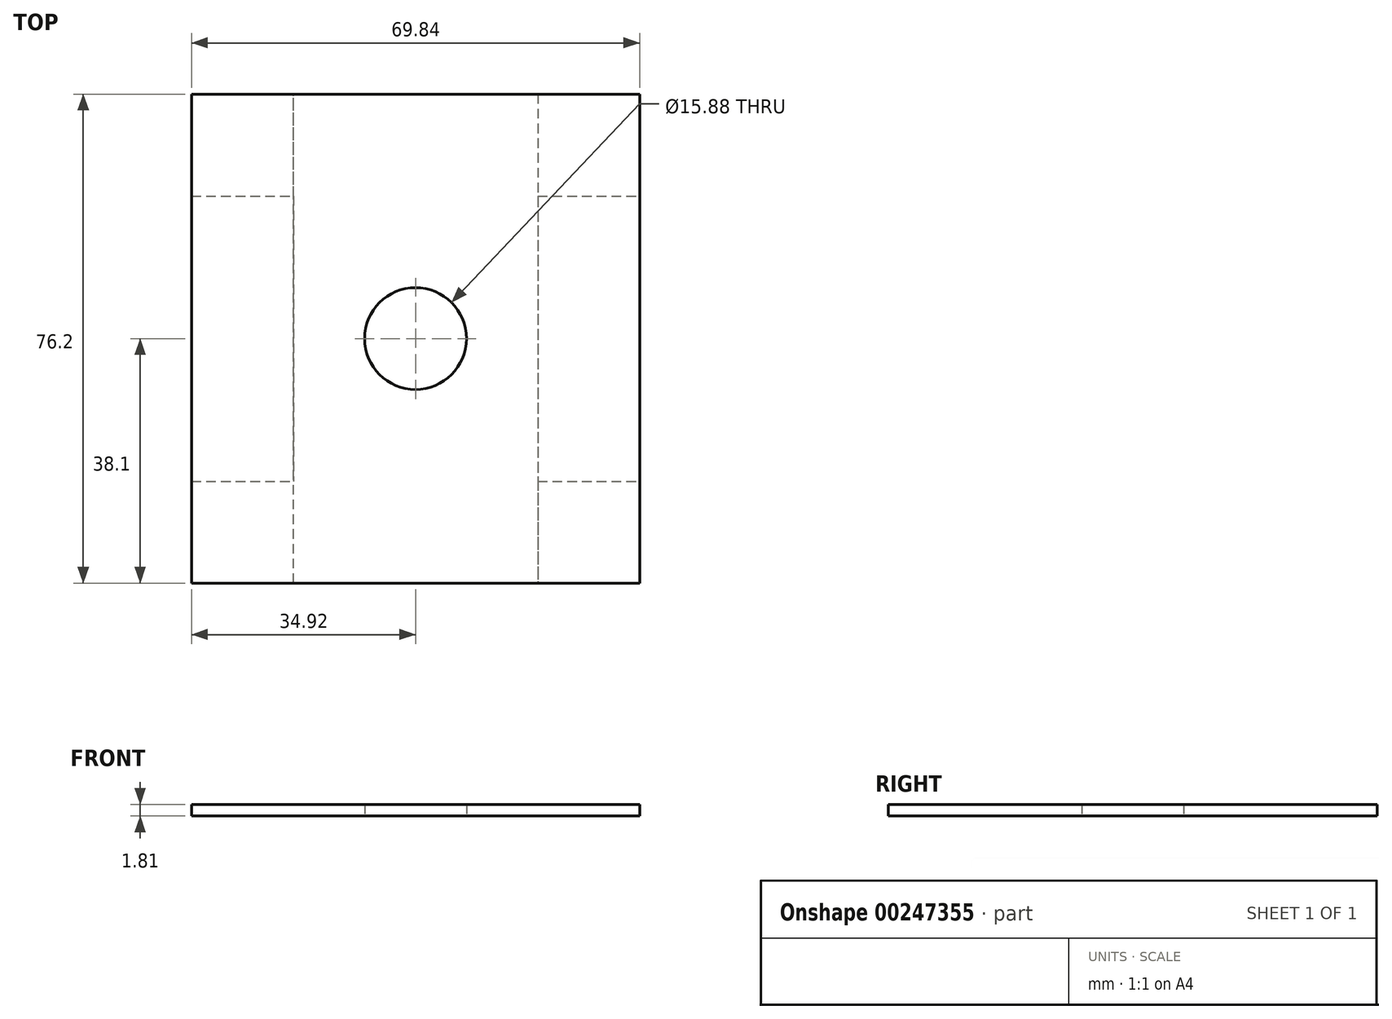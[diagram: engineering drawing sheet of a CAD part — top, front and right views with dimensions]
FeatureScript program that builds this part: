
annotation { "Feature Type Name" : "Feature", "Feature Type Description" : "" }
export const myFeature = defineFeature(function(context is Context, id is Id, definition is map)
    precondition{}
    {
        {
            var Q0;
            Q0=qCreatedBy(makeId("Top.planeOp"),FACE);
            var sketch = newSketch(context, id + "F0", { "sketchPlane" : qUnion([Q0])});
            skLineSegment(sketch, "E0.bottom", {"start": v(63.5, -38.1) * mm, "end": v(-63.5, -38.1) * mm});
            skLineSegment(sketch, "E0.top", {"start": v(34.93, 38.1) * mm, "end": v(19.05, 38.1) * mm});
            skLineSegment(sketch, "E0.left", {"start": v(63.5, -38.1) * mm, "end": v(63.5, -12.7) * mm});
            skLineSegment(sketch, "E0.right", {"start": v(-63.5, -38.1) * mm, "end": v(-63.5, -12.7) * mm});
            skPoint(sketch, "E0.middle", {"position": v(0, 0) * mm});
            skLineSegment(sketch, "E1", {"start": v(-63.5, 12.7) * mm, "end": v(-42.86, 12.7) * mm});
            skLineSegment(sketch, "E2", {"start": v(-42.86, 12.7) * mm, "end": v(-42.86, -12.7) * mm});
            skLineSegment(sketch, "E3", {"start": v(-42.86, -12.7) * mm, "end": v(-63.5, -12.7) * mm});
            skLineSegment(sketch, "E4", {"start": v(63.5, 12.7) * mm, "end": v(42.86, 12.7) * mm});
            skLineSegment(sketch, "E5", {"start": v(42.86, 12.7) * mm, "end": v(42.86, -12.7) * mm});
            skLineSegment(sketch, "E6", {"start": v(42.86, -12.7) * mm, "end": v(63.5, -12.7) * mm});
            skLineSegment(sketch, "E7.trimOffspring", {"start": v(-63.5, 12.7) * mm, "end": v(-63.5, 38.1) * mm});
            skLineSegment(sketch, "E8.trimOffspring", {"start": v(63.5, 12.7) * mm, "end": v(63.5, 38.1) * mm});
            skCircle(sketch, "E9", {"center": v(0, 0) * mm, "radius": 7.94 * mm});
            skLineSegment(sketch, "E10", {"start": v(-34.93, 38.1) * mm, "end": v(-34.93, 22.23) * mm});
            skLineSegment(sketch, "E11", {"start": v(-19.05, -38.1) * mm, "end": v(-19.05, -22.23) * mm});
            skLineSegment(sketch, "E12", {"start": v(19.05, 38.1) * mm, "end": v(19.05, 22.23) * mm});
            skLineSegment(sketch, "E13", {"start": v(34.92, 38.1) * mm, "end": v(34.92, 22.23) * mm});
            skLineSegment(sketch, "E14", {"start": v(-63.5, 38.1) * mm, "end": v(-34.93, 38.1) * mm});
            skLineSegment(sketch, "E15", {"start": v(34.93, 38.1) * mm, "end": v(63.5, 38.1) * mm});
            skLineSegment(sketch, "E16.trimOffspring", {"start": v(-19.05, 38.1) * mm, "end": v(-34.93, 38.1) * mm});
            skLineSegment(sketch, "E17", {"start": v(-19.05, 38.1) * mm, "end": v(19.05, 38.1) * mm});
            skLineSegment(sketch, "E18", {"start": v(-34.93, 22.22) * mm, "end": v(-19.05, 22.23) * mm});
            skLineSegment(sketch, "E19", {"start": v(-34.92, -22.23) * mm, "end": v(-19.05, -22.23) * mm});
            skLineSegment(sketch, "E20", {"start": v(19.05, -22.22) * mm, "end": v(34.92, -22.22) * mm});
            skLineSegment(sketch, "E21", {"start": v(19.05, 22.23) * mm, "end": v(34.92, 22.23) * mm});
            skLineSegment(sketch, "E22.trimOffspring", {"start": v(-34.92, -22.23) * mm, "end": v(-34.92, -38.1) * mm});
            skLineSegment(sketch, "E23.trimOffspring", {"start": v(-19.05, 22.23) * mm, "end": v(-19.05, 38.1) * mm});
            skLineSegment(sketch, "E24.trimOffspring", {"start": v(19.05, -22.22) * mm, "end": v(19.05, -38.1) * mm});
            skLineSegment(sketch, "E25.trimOffspring", {"start": v(34.92, -22.22) * mm, "end": v(34.92, -38.1) * mm});
            skLineSegment(sketch, "E26", {"start": v(-34.93, 22.22) * mm, "end": v(-34.92, -22.23) * mm});
            skLineSegment(sketch, "E27", {"start": v(-19.05, 22.23) * mm, "end": v(-19.05, -22.23) * mm});
            skLineSegment(sketch, "E28", {"start": v(19.05, 22.23) * mm, "end": v(19.05, -22.22) * mm});
            skLineSegment(sketch, "E29", {"start": v(34.92, 22.23) * mm, "end": v(34.92, -22.22) * mm});
            skSolve(sketch);
        }
        {
            var Q0;
            Q0=makeQuery(id+"F0.imprint","IMPRINT",FACE,{"disambiguationData":[TD([[makeQuery(id+"F0.imprint","IMPRINT",EDGE,{"derivedFrom":sQuery(id+"F0.wireOp",EDGE,"E20")}),-1.0]])]});
            var Q1;
            Q1=makeQuery(id+"F0.imprint","IMPRINT",FACE,{"disambiguationData":[TD([[makeQuery(id+"F0.imprint","IMPRINT",EDGE,{"derivedFrom":sQuery(id+"F0.wireOp",EDGE,"E20")}),1.0]])]});
            var Q2;
            {var subQ0=sQuery(id+"F0.wireOp",EDGE,"E0.left");Q2=makeQuery(id+"F0.imprint","IMPRINT",FACE,{"disambiguationData":[TD([[makeQuery(id+"F0.imprint","IMPRINT",EDGE,{"derivedFrom":subQ0}),1.0]])]});}
            var Q3;
            Q3=makeQuery(id+"F0.imprint","IMPRINT",FACE,{"disambiguationData":[TD([[makeQuery(id+"F0.imprint","IMPRINT",EDGE,{"derivedFrom":sQuery(id+"F0.wireOp",EDGE,"E9")}),-1.0]])]});
            var Q4;
            {var subQ0=sQuery(id+"F0.wireOp",EDGE,"E11");Q4=makeQuery(id+"F0.imprint","IMPRINT",FACE,{"disambiguationData":[TD([[makeQuery(id+"F0.imprint","IMPRINT",EDGE,{"derivedFrom":subQ0}),1.0]])]});}
            var Q5;
            Q5=makeQuery(id+"F0.imprint","IMPRINT",FACE,{"disambiguationData":[TD([[makeQuery(id+"F0.imprint","IMPRINT",EDGE,{"derivedFrom":sQuery(id+"F0.wireOp",EDGE,"E0.top")}),1.0]])]});
            var Q6;
            {var subQ1=sQuery(id+"F0.wireOp",EDGE,"E0.right");Q6=makeQuery(id+"F0.imprint","IMPRINT",FACE,{"disambiguationData":[TD([[makeQuery(id+"F0.imprint","IMPRINT",EDGE,{"derivedFrom":subQ1}),-1.0]])]});}
            var Q7;
            Q7=makeQuery(id+"F0.imprint","IMPRINT",FACE,{"disambiguationData":[TD([[makeQuery(id+"F0.imprint","IMPRINT",EDGE,{"derivedFrom":sQuery(id+"F0.wireOp",EDGE,"E10")}),1.0]])]});
            var Q8;
            Q8=makeQuery(id+"F0.imprint","IMPRINT",FACE,{"disambiguationData":[TD([[makeQuery(id+"F0.imprint","IMPRINT",EDGE,{"derivedFrom":sQuery(id+"F0.wireOp",EDGE,"E18")}),-1.0]])]});
            extrude(context, id + "F1", {"entities" : qUnion([Q0, Q1, Q2, Q3, Q4, Q5, Q6, Q7, Q8]), "depth" : ((3 + 5 / 8) / 2) * mm});
        }
        {
            var Q0;
            {var subQ0=sQuery(id+"F0.wireOp",EDGE,"E0.left");Q0=makeQuery(id+"F0.imprint","IMPRINT",FACE,{"disambiguationData":[TD([[makeQuery(id+"F0.imprint","IMPRINT",EDGE,{"derivedFrom":subQ0}),1.0]])]});}
            var Q1;
            {var subQ1=sQuery(id+"F0.wireOp",EDGE,"E0.right");Q1=makeQuery(id+"F0.imprint","IMPRINT",FACE,{"disambiguationData":[TD([[makeQuery(id+"F0.imprint","IMPRINT",EDGE,{"derivedFrom":subQ1}),-1.0]])]});}
            extrude(context, id + "F2", {"entities" : qUnion([Q0, Q1]), "operationType" : NewBodyOperationType.REMOVE, "depth" : 30.16 * mm});
        }
        {
            var Q0;
            Q0=makeQuery(id+"F0.imprint","IMPRINT",FACE,{"disambiguationData":[TD([[makeQuery(id+"F0.imprint","IMPRINT",EDGE,{"derivedFrom":sQuery(id+"F0.wireOp",EDGE,"E9")}),-1.0]])]});
            extrude(context, id + "F3", {"entities" : qUnion([Q0]), "operationType" : NewBodyOperationType.REMOVE, "depth" : (1 + 1 / 2) / 50.8 * mm});
        }
        {
            var Q0;
            Q0=makeQuery(id+"F0.imprint","IMPRINT",FACE,{"disambiguationData":[TD([[makeQuery(id+"F0.imprint","IMPRINT",EDGE,{"derivedFrom":sQuery(id+"F0.wireOp",EDGE,"E18")}),-1.0]])]});
            var Q1;
            Q1=makeQuery(id+"F0.imprint","IMPRINT",FACE,{"disambiguationData":[TD([[makeQuery(id+"F0.imprint","IMPRINT",EDGE,{"derivedFrom":sQuery(id+"F0.wireOp",EDGE,"E20")}),1.0]])]});
            extrude(context, id + "F4", {"entities" : qUnion([Q0, Q1]), "operationType" : NewBodyOperationType.REMOVE, "depth" : (3 / 4) / 50.8 * mm});
        }
    });
